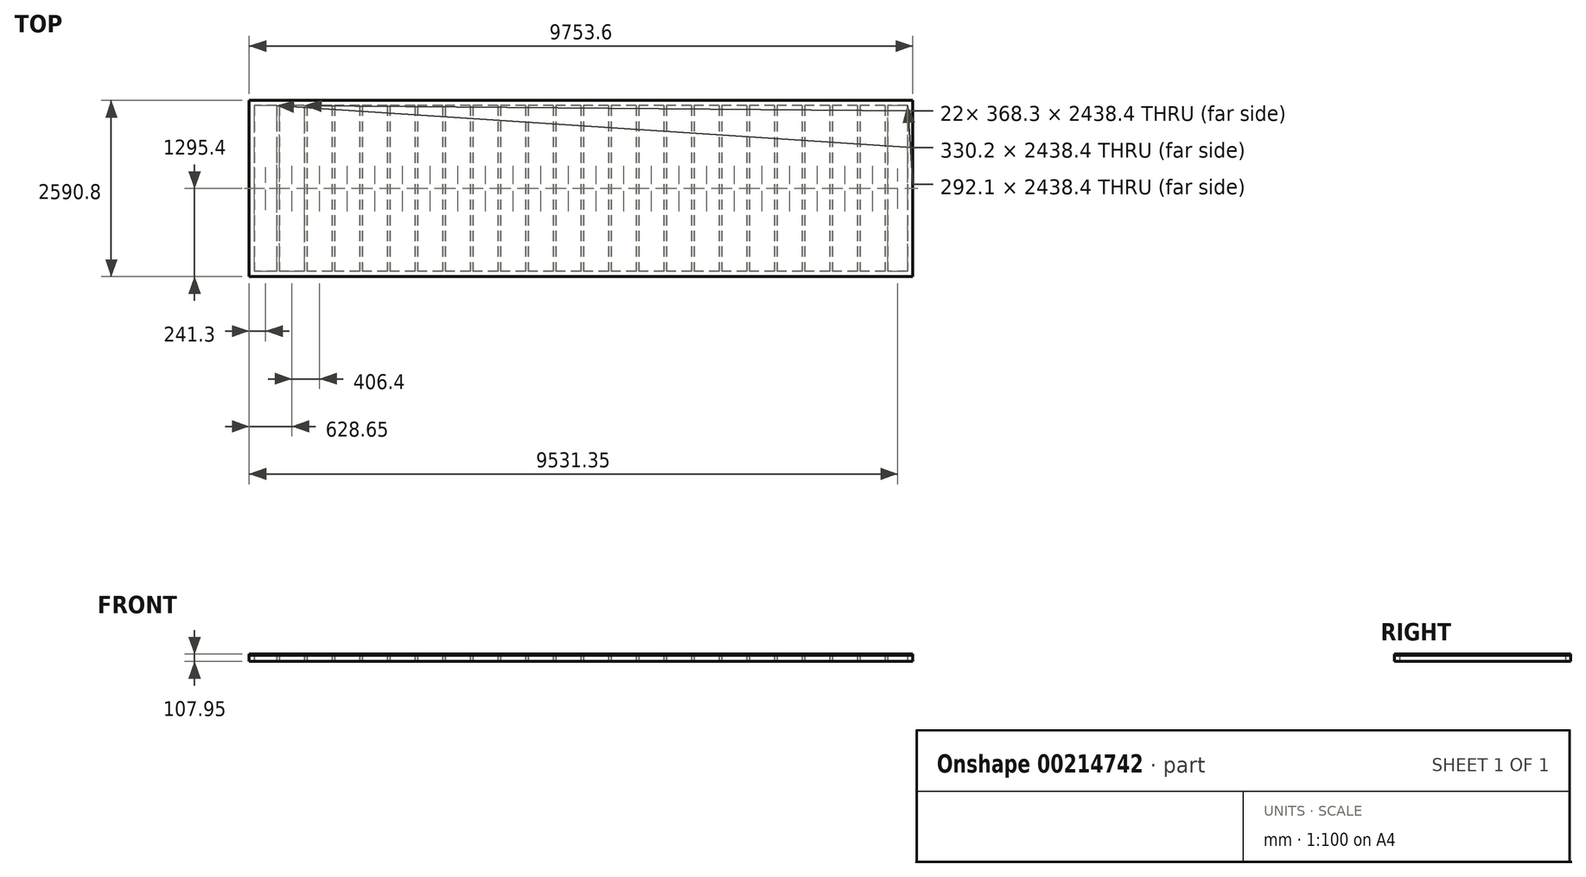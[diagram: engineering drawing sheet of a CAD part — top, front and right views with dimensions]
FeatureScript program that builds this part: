
annotation { "Feature Type Name" : "Feature", "Feature Type Description" : "" }
export const myFeature = defineFeature(function(context is Context, id is Id, definition is map)
    precondition{}
    {
        {
            var Q0;
            Q0=qCreatedBy(makeId("Right.planeOp"),FACE);
            var sketch = newSketch(context, id + "F0", { "sketchPlane" : qUnion([Q0])});
            skLineSegment(sketch, "E0.bottom", {"start": v(19.05, -44.45) * mm, "end": v(-19.05, -44.45) * mm});
            skLineSegment(sketch, "E0.top", {"start": v(19.05, 44.45) * mm, "end": v(-19.05, 44.45) * mm});
            skLineSegment(sketch, "E0.left", {"start": v(19.05, -44.45) * mm, "end": v(19.05, 44.45) * mm});
            skLineSegment(sketch, "E0.right", {"start": v(-19.05, -44.45) * mm, "end": v(-19.05, 44.45) * mm});
            skPoint(sketch, "E0.middle", {"position": v(0, 0) * mm});
            skSolve(sketch);
        }
        {
            var Q0;
            Q0 = qSketchRegion(id + "F0", true);
            extrude(context, id + "F1", {"entities" : qUnion([Q0]), "depth" : 9753.6 * mm, "offsetDistance" : 25.4 * mm});
        }
        {
            var Q0;
            Q0=makeQuery(id+"F1.opExtrude","SWEPT_FACE",FACE,{"disambiguationData":[OSD([sQuery(id+"F0.wireOp",EDGE,"E0.left")])]});
            var sketch = newSketch(context, id + "F2", { "sketchPlane" : qUnion([Q0])});
            skLineSegment(sketch, "E1.bottom", {"start": v(0, 44.45) * mm, "end": v(-38.1, 44.45) * mm});
            skLineSegment(sketch, "E1.top", {"start": v(0, -44.45) * mm, "end": v(-38.1, -44.45) * mm});
            skLineSegment(sketch, "E1.left", {"start": v(0, 44.45) * mm, "end": v(0, -44.45) * mm});
            skLineSegment(sketch, "E1.right", {"start": v(-38.1, 44.45) * mm, "end": v(-38.1, -44.45) * mm});
            skLineSegment(sketch, "E2.1.0.0", {"start": v(-444.5, 44.45) * mm, "end": v(-444.5, -44.45) * mm});
            skLineSegment(sketch, "E2.1.0.1", {"start": v(-406.4, -44.45) * mm, "end": v(-444.5, -44.45) * mm});
            skLineSegment(sketch, "E2.1.0.2", {"start": v(-406.4, 44.45) * mm, "end": v(-406.4, -44.45) * mm});
            skLineSegment(sketch, "E2.1.0.3", {"start": v(-406.4, 44.45) * mm, "end": v(-444.5, 44.45) * mm});
            skLineSegment(sketch, "E2.2.0.0", {"start": v(-850.9, 44.45) * mm, "end": v(-850.9, -44.45) * mm});
            skLineSegment(sketch, "E2.2.0.1", {"start": v(-812.8, -44.45) * mm, "end": v(-850.9, -44.45) * mm});
            skLineSegment(sketch, "E2.2.0.2", {"start": v(-812.8, 44.45) * mm, "end": v(-812.8, -44.45) * mm});
            skLineSegment(sketch, "E2.2.0.3", {"start": v(-812.8, 44.45) * mm, "end": v(-850.9, 44.45) * mm});
            skLineSegment(sketch, "E2.3.0.0", {"start": v(-1257.3, 44.45) * mm, "end": v(-1257.3, -44.45) * mm});
            skLineSegment(sketch, "E2.3.0.1", {"start": v(-1219.2, -44.45) * mm, "end": v(-1257.3, -44.45) * mm});
            skLineSegment(sketch, "E2.3.0.2", {"start": v(-1219.2, 44.45) * mm, "end": v(-1219.2, -44.45) * mm});
            skLineSegment(sketch, "E2.3.0.3", {"start": v(-1219.2, 44.45) * mm, "end": v(-1257.3, 44.45) * mm});
            skLineSegment(sketch, "E2.4.0.0", {"start": v(-1663.7, 44.45) * mm, "end": v(-1663.7, -44.45) * mm});
            skLineSegment(sketch, "E2.4.0.1", {"start": v(-1625.6, -44.45) * mm, "end": v(-1663.7, -44.45) * mm});
            skLineSegment(sketch, "E2.4.0.2", {"start": v(-1625.6, 44.45) * mm, "end": v(-1625.6, -44.45) * mm});
            skLineSegment(sketch, "E2.4.0.3", {"start": v(-1625.6, 44.45) * mm, "end": v(-1663.7, 44.45) * mm});
            skLineSegment(sketch, "E2.5.0.0", {"start": v(-2070.1, 44.45) * mm, "end": v(-2070.1, -44.45) * mm});
            skLineSegment(sketch, "E2.5.0.1", {"start": v(-2032, -44.45) * mm, "end": v(-2070.1, -44.45) * mm});
            skLineSegment(sketch, "E2.5.0.2", {"start": v(-2032, 44.45) * mm, "end": v(-2032, -44.45) * mm});
            skLineSegment(sketch, "E2.5.0.3", {"start": v(-2032, 44.45) * mm, "end": v(-2070.1, 44.45) * mm});
            skLineSegment(sketch, "E2.6.0.0", {"start": v(-2476.5, 44.45) * mm, "end": v(-2476.5, -44.45) * mm});
            skLineSegment(sketch, "E2.6.0.1", {"start": v(-2438.4, -44.45) * mm, "end": v(-2476.5, -44.45) * mm});
            skLineSegment(sketch, "E2.6.0.2", {"start": v(-2438.4, 44.45) * mm, "end": v(-2438.4, -44.45) * mm});
            skLineSegment(sketch, "E2.6.0.3", {"start": v(-2438.4, 44.45) * mm, "end": v(-2476.5, 44.45) * mm});
            skLineSegment(sketch, "E2.7.0.0", {"start": v(-2882.9, 44.45) * mm, "end": v(-2882.9, -44.45) * mm});
            skLineSegment(sketch, "E2.7.0.1", {"start": v(-2844.8, -44.45) * mm, "end": v(-2882.9, -44.45) * mm});
            skLineSegment(sketch, "E2.7.0.2", {"start": v(-2844.8, 44.45) * mm, "end": v(-2844.8, -44.45) * mm});
            skLineSegment(sketch, "E2.7.0.3", {"start": v(-2844.8, 44.45) * mm, "end": v(-2882.9, 44.45) * mm});
            skLineSegment(sketch, "E2.8.0.0", {"start": v(-3289.3, 44.45) * mm, "end": v(-3289.3, -44.45) * mm});
            skLineSegment(sketch, "E2.8.0.1", {"start": v(-3251.2, -44.45) * mm, "end": v(-3289.3, -44.45) * mm});
            skLineSegment(sketch, "E2.8.0.2", {"start": v(-3251.2, 44.45) * mm, "end": v(-3251.2, -44.45) * mm});
            skLineSegment(sketch, "E2.8.0.3", {"start": v(-3251.2, 44.45) * mm, "end": v(-3289.3, 44.45) * mm});
            skLineSegment(sketch, "E2.9.0.0", {"start": v(-3695.7, 44.45) * mm, "end": v(-3695.7, -44.45) * mm});
            skLineSegment(sketch, "E2.9.0.1", {"start": v(-3657.6, -44.45) * mm, "end": v(-3695.7, -44.45) * mm});
            skLineSegment(sketch, "E2.9.0.2", {"start": v(-3657.6, 44.45) * mm, "end": v(-3657.6, -44.45) * mm});
            skLineSegment(sketch, "E2.9.0.3", {"start": v(-3657.6, 44.45) * mm, "end": v(-3695.7, 44.45) * mm});
            skLineSegment(sketch, "E2.10.0.0", {"start": v(-4102.1, 44.45) * mm, "end": v(-4102.1, -44.45) * mm});
            skLineSegment(sketch, "E2.10.0.1", {"start": v(-4064, -44.45) * mm, "end": v(-4102.1, -44.45) * mm});
            skLineSegment(sketch, "E2.10.0.2", {"start": v(-4064, 44.45) * mm, "end": v(-4064, -44.45) * mm});
            skLineSegment(sketch, "E2.10.0.3", {"start": v(-4064, 44.45) * mm, "end": v(-4102.1, 44.45) * mm});
            skLineSegment(sketch, "E2.11.0.0", {"start": v(-4508.5, 44.45) * mm, "end": v(-4508.5, -44.45) * mm});
            skLineSegment(sketch, "E2.11.0.1", {"start": v(-4470.4, -44.45) * mm, "end": v(-4508.5, -44.45) * mm});
            skLineSegment(sketch, "E2.11.0.2", {"start": v(-4470.4, 44.45) * mm, "end": v(-4470.4, -44.45) * mm});
            skLineSegment(sketch, "E2.11.0.3", {"start": v(-4470.4, 44.45) * mm, "end": v(-4508.5, 44.45) * mm});
            skLineSegment(sketch, "E2.12.0.0", {"start": v(-4914.9, 44.45) * mm, "end": v(-4914.9, -44.45) * mm});
            skLineSegment(sketch, "E2.12.0.1", {"start": v(-4876.8, -44.45) * mm, "end": v(-4914.9, -44.45) * mm});
            skLineSegment(sketch, "E2.12.0.2", {"start": v(-4876.8, 44.45) * mm, "end": v(-4876.8, -44.45) * mm});
            skLineSegment(sketch, "E2.12.0.3", {"start": v(-4876.8, 44.45) * mm, "end": v(-4914.9, 44.45) * mm});
            skLineSegment(sketch, "E2.13.0.0", {"start": v(-5321.3, 44.45) * mm, "end": v(-5321.3, -44.45) * mm});
            skLineSegment(sketch, "E2.13.0.1", {"start": v(-5283.2, -44.45) * mm, "end": v(-5321.3, -44.45) * mm});
            skLineSegment(sketch, "E2.13.0.2", {"start": v(-5283.2, 44.45) * mm, "end": v(-5283.2, -44.45) * mm});
            skLineSegment(sketch, "E2.13.0.3", {"start": v(-5283.2, 44.45) * mm, "end": v(-5321.3, 44.45) * mm});
            skLineSegment(sketch, "E2.14.0.0", {"start": v(-5727.7, 44.45) * mm, "end": v(-5727.7, -44.45) * mm});
            skLineSegment(sketch, "E2.14.0.1", {"start": v(-5689.6, -44.45) * mm, "end": v(-5727.7, -44.45) * mm});
            skLineSegment(sketch, "E2.14.0.2", {"start": v(-5689.6, 44.45) * mm, "end": v(-5689.6, -44.45) * mm});
            skLineSegment(sketch, "E2.14.0.3", {"start": v(-5689.6, 44.45) * mm, "end": v(-5727.7, 44.45) * mm});
            skLineSegment(sketch, "E2.15.0.0", {"start": v(-6134.1, 44.45) * mm, "end": v(-6134.1, -44.45) * mm});
            skLineSegment(sketch, "E2.15.0.1", {"start": v(-6096, -44.45) * mm, "end": v(-6134.1, -44.45) * mm});
            skLineSegment(sketch, "E2.15.0.2", {"start": v(-6096, 44.45) * mm, "end": v(-6096, -44.45) * mm});
            skLineSegment(sketch, "E2.15.0.3", {"start": v(-6096, 44.45) * mm, "end": v(-6134.1, 44.45) * mm});
            skLineSegment(sketch, "E2.16.0.0", {"start": v(-6540.5, 44.45) * mm, "end": v(-6540.5, -44.45) * mm});
            skLineSegment(sketch, "E2.16.0.1", {"start": v(-6502.4, -44.45) * mm, "end": v(-6540.5, -44.45) * mm});
            skLineSegment(sketch, "E2.16.0.2", {"start": v(-6502.4, 44.45) * mm, "end": v(-6502.4, -44.45) * mm});
            skLineSegment(sketch, "E2.16.0.3", {"start": v(-6502.4, 44.45) * mm, "end": v(-6540.5, 44.45) * mm});
            skLineSegment(sketch, "E2.17.0.0", {"start": v(-6946.9, 44.45) * mm, "end": v(-6946.9, -44.45) * mm});
            skLineSegment(sketch, "E2.17.0.1", {"start": v(-6908.8, -44.45) * mm, "end": v(-6946.9, -44.45) * mm});
            skLineSegment(sketch, "E2.17.0.2", {"start": v(-6908.8, 44.45) * mm, "end": v(-6908.8, -44.45) * mm});
            skLineSegment(sketch, "E2.17.0.3", {"start": v(-6908.8, 44.45) * mm, "end": v(-6946.9, 44.45) * mm});
            skLineSegment(sketch, "E2.18.0.0", {"start": v(-7353.3, 44.45) * mm, "end": v(-7353.3, -44.45) * mm});
            skLineSegment(sketch, "E2.18.0.1", {"start": v(-7315.2, -44.45) * mm, "end": v(-7353.3, -44.45) * mm});
            skLineSegment(sketch, "E2.18.0.2", {"start": v(-7315.2, 44.45) * mm, "end": v(-7315.2, -44.45) * mm});
            skLineSegment(sketch, "E2.18.0.3", {"start": v(-7315.2, 44.45) * mm, "end": v(-7353.3, 44.45) * mm});
            skLineSegment(sketch, "E2.19.0.0", {"start": v(-7759.7, 44.45) * mm, "end": v(-7759.7, -44.45) * mm});
            skLineSegment(sketch, "E2.19.0.1", {"start": v(-7721.6, -44.45) * mm, "end": v(-7759.7, -44.45) * mm});
            skLineSegment(sketch, "E2.19.0.2", {"start": v(-7721.6, 44.45) * mm, "end": v(-7721.6, -44.45) * mm});
            skLineSegment(sketch, "E2.19.0.3", {"start": v(-7721.6, 44.45) * mm, "end": v(-7759.7, 44.45) * mm});
            skLineSegment(sketch, "E2.20.0.0", {"start": v(-8166.1, 44.45) * mm, "end": v(-8166.1, -44.45) * mm});
            skLineSegment(sketch, "E2.20.0.1", {"start": v(-8128, -44.45) * mm, "end": v(-8166.1, -44.45) * mm});
            skLineSegment(sketch, "E2.20.0.2", {"start": v(-8128, 44.45) * mm, "end": v(-8128, -44.45) * mm});
            skLineSegment(sketch, "E2.20.0.3", {"start": v(-8128, 44.45) * mm, "end": v(-8166.1, 44.45) * mm});
            skLineSegment(sketch, "E2.21.0.0", {"start": v(-8572.5, 44.45) * mm, "end": v(-8572.5, -44.45) * mm});
            skLineSegment(sketch, "E2.21.0.1", {"start": v(-8534.4, -44.45) * mm, "end": v(-8572.5, -44.45) * mm});
            skLineSegment(sketch, "E2.21.0.2", {"start": v(-8534.4, 44.45) * mm, "end": v(-8534.4, -44.45) * mm});
            skLineSegment(sketch, "E2.21.0.3", {"start": v(-8534.4, 44.45) * mm, "end": v(-8572.5, 44.45) * mm});
            skLineSegment(sketch, "E2.22.0.0", {"start": v(-8978.9, 44.45) * mm, "end": v(-8978.9, -44.45) * mm});
            skLineSegment(sketch, "E2.22.0.1", {"start": v(-8940.8, -44.45) * mm, "end": v(-8978.9, -44.45) * mm});
            skLineSegment(sketch, "E2.22.0.2", {"start": v(-8940.8, 44.45) * mm, "end": v(-8940.8, -44.45) * mm});
            skLineSegment(sketch, "E2.22.0.3", {"start": v(-8940.8, 44.45) * mm, "end": v(-8978.9, 44.45) * mm});
            skLineSegment(sketch, "E2.23.0.0", {"start": v(-9385.3, 44.45) * mm, "end": v(-9385.3, -44.45) * mm});
            skLineSegment(sketch, "E2.23.0.1", {"start": v(-9347.2, -44.45) * mm, "end": v(-9385.3, -44.45) * mm});
            skLineSegment(sketch, "E2.23.0.2", {"start": v(-9347.2, 44.45) * mm, "end": v(-9347.2, -44.45) * mm});
            skLineSegment(sketch, "E2.23.0.3", {"start": v(-9347.2, 44.45) * mm, "end": v(-9385.3, 44.45) * mm});
            skLineSegment(sketch, "E2.direction1", {"start": v(-38.1, -44.45) * mm, "end": v(-444.5, -44.45) * mm, "construction": true});
            skSolve(sketch);
        }
        {
            var Q0;
            Q0=makeQuery(id+"F2.imprint","IMPRINT",FACE,{"disambiguationData":[TD([[makeQuery(id+"F2.imprint","IMPRINT",EDGE,{"derivedFrom":sQuery(id+"F2.wireOp",EDGE,"E2.23.0.0")}),1.0]])]});
            var Q1;
            Q1=makeQuery(id+"F2.imprint","IMPRINT",FACE,{"disambiguationData":[TD([[makeQuery(id+"F2.imprint","IMPRINT",EDGE,{"derivedFrom":sQuery(id+"F2.wireOp",EDGE,"E2.22.0.0")}),1.0]])]});
            var Q2;
            Q2=makeQuery(id+"F2.imprint","IMPRINT",FACE,{"disambiguationData":[TD([[makeQuery(id+"F2.imprint","IMPRINT",EDGE,{"derivedFrom":sQuery(id+"F2.wireOp",EDGE,"E2.21.0.0")}),1.0]])]});
            var Q3;
            Q3=makeQuery(id+"F2.imprint","IMPRINT",FACE,{"disambiguationData":[TD([[makeQuery(id+"F2.imprint","IMPRINT",EDGE,{"derivedFrom":sQuery(id+"F2.wireOp",EDGE,"E2.20.0.0")}),1.0]])]});
            var Q4;
            Q4=makeQuery(id+"F2.imprint","IMPRINT",FACE,{"disambiguationData":[TD([[makeQuery(id+"F2.imprint","IMPRINT",EDGE,{"derivedFrom":sQuery(id+"F2.wireOp",EDGE,"E2.19.0.0")}),1.0]])]});
            var Q5;
            Q5=makeQuery(id+"F2.imprint","IMPRINT",FACE,{"disambiguationData":[TD([[makeQuery(id+"F2.imprint","IMPRINT",EDGE,{"derivedFrom":sQuery(id+"F2.wireOp",EDGE,"E2.18.0.0")}),1.0]])]});
            var Q6;
            Q6=makeQuery(id+"F2.imprint","IMPRINT",FACE,{"disambiguationData":[TD([[makeQuery(id+"F2.imprint","IMPRINT",EDGE,{"derivedFrom":sQuery(id+"F2.wireOp",EDGE,"E2.17.0.0")}),1.0]])]});
            var Q7;
            Q7=makeQuery(id+"F2.imprint","IMPRINT",FACE,{"disambiguationData":[TD([[makeQuery(id+"F2.imprint","IMPRINT",EDGE,{"derivedFrom":sQuery(id+"F2.wireOp",EDGE,"E2.16.0.0")}),1.0]])]});
            var Q8;
            Q8=makeQuery(id+"F2.imprint","IMPRINT",FACE,{"disambiguationData":[TD([[makeQuery(id+"F2.imprint","IMPRINT",EDGE,{"derivedFrom":sQuery(id+"F2.wireOp",EDGE,"E2.15.0.0")}),1.0]])]});
            var Q9;
            Q9=makeQuery(id+"F2.imprint","IMPRINT",FACE,{"disambiguationData":[TD([[makeQuery(id+"F2.imprint","IMPRINT",EDGE,{"derivedFrom":sQuery(id+"F2.wireOp",EDGE,"E2.14.0.0")}),1.0]])]});
            var Q10;
            Q10=makeQuery(id+"F2.imprint","IMPRINT",FACE,{"disambiguationData":[TD([[makeQuery(id+"F2.imprint","IMPRINT",EDGE,{"derivedFrom":sQuery(id+"F2.wireOp",EDGE,"E2.13.0.0")}),1.0]])]});
            var Q11;
            Q11=makeQuery(id+"F2.imprint","IMPRINT",FACE,{"disambiguationData":[TD([[makeQuery(id+"F2.imprint","IMPRINT",EDGE,{"derivedFrom":sQuery(id+"F2.wireOp",EDGE,"E2.12.0.0")}),1.0]])]});
            var Q12;
            Q12=makeQuery(id+"F2.imprint","IMPRINT",FACE,{"disambiguationData":[TD([[makeQuery(id+"F2.imprint","IMPRINT",EDGE,{"derivedFrom":sQuery(id+"F2.wireOp",EDGE,"E2.11.0.0")}),1.0]])]});
            var Q13;
            Q13=makeQuery(id+"F2.imprint","IMPRINT",FACE,{"disambiguationData":[TD([[makeQuery(id+"F2.imprint","IMPRINT",EDGE,{"derivedFrom":sQuery(id+"F2.wireOp",EDGE,"E2.10.0.0")}),1.0]])]});
            var Q14;
            Q14=makeQuery(id+"F2.imprint","IMPRINT",FACE,{"disambiguationData":[TD([[makeQuery(id+"F2.imprint","IMPRINT",EDGE,{"derivedFrom":sQuery(id+"F2.wireOp",EDGE,"E2.9.0.0")}),1.0]])]});
            var Q15;
            Q15=makeQuery(id+"F2.imprint","IMPRINT",FACE,{"disambiguationData":[TD([[makeQuery(id+"F2.imprint","IMPRINT",EDGE,{"derivedFrom":sQuery(id+"F2.wireOp",EDGE,"E2.8.0.0")}),1.0]])]});
            var Q16;
            Q16=makeQuery(id+"F2.imprint","IMPRINT",FACE,{"disambiguationData":[TD([[makeQuery(id+"F2.imprint","IMPRINT",EDGE,{"derivedFrom":sQuery(id+"F2.wireOp",EDGE,"E2.7.0.0")}),1.0]])]});
            var Q17;
            Q17=makeQuery(id+"F2.imprint","IMPRINT",FACE,{"disambiguationData":[TD([[makeQuery(id+"F2.imprint","IMPRINT",EDGE,{"derivedFrom":sQuery(id+"F2.wireOp",EDGE,"E2.6.0.0")}),1.0]])]});
            var Q18;
            Q18=makeQuery(id+"F2.imprint","IMPRINT",FACE,{"disambiguationData":[TD([[makeQuery(id+"F2.imprint","IMPRINT",EDGE,{"derivedFrom":sQuery(id+"F2.wireOp",EDGE,"E2.5.0.0")}),1.0]])]});
            var Q19;
            Q19=makeQuery(id+"F2.imprint","IMPRINT",FACE,{"disambiguationData":[TD([[makeQuery(id+"F2.imprint","IMPRINT",EDGE,{"derivedFrom":sQuery(id+"F2.wireOp",EDGE,"E2.4.0.0")}),1.0]])]});
            var Q20;
            Q20=makeQuery(id+"F2.imprint","IMPRINT",FACE,{"disambiguationData":[TD([[makeQuery(id+"F2.imprint","IMPRINT",EDGE,{"derivedFrom":sQuery(id+"F2.wireOp",EDGE,"E2.3.0.0")}),1.0]])]});
            var Q21;
            Q21=makeQuery(id+"F2.imprint","IMPRINT",FACE,{"disambiguationData":[TD([[makeQuery(id+"F2.imprint","IMPRINT",EDGE,{"derivedFrom":sQuery(id+"F2.wireOp",EDGE,"E2.2.0.0")}),1.0]])]});
            var Q22;
            Q22=makeQuery(id+"F2.imprint","IMPRINT",FACE,{"disambiguationData":[TD([[makeQuery(id+"F2.imprint","IMPRINT",EDGE,{"derivedFrom":sQuery(id+"F2.wireOp",EDGE,"E2.1.0.0")}),1.0]])]});
            var Q23;
            Q23=makeQuery(id+"F2.imprint","IMPRINT",FACE,{"disambiguationData":[TD([[makeQuery(id+"F2.imprint","IMPRINT",EDGE,{"derivedFrom":sQuery(id+"F2.wireOp",EDGE,"E1.bottom")}),-1.0]])]});
            extrude(context, id + "F3", {"entities" : qUnion([Q0, Q1, Q2, Q3, Q4, Q5, Q6, Q7, Q8, Q9, Q10, Q11, Q12, Q13, Q14, Q15, Q16, Q17, Q18, Q19, Q20, Q21, Q22, Q23]), "operationType" : NewBodyOperationType.ADD, "depth" : 2438.4 * mm, "offsetDistance" : 25.4 * mm});
        }
        {
            var Q0;
            {var subQ0=sQuery(id+"F0.wireOp",EDGE,"E0.left");Q0=makeQuery(id+"F3.boolean.opBoolean","SPLIT",FACE,{"disambiguationData":[TD([makeQuery(id+"F3.opExtrude","SWEPT_FACE",FACE,{"disambiguationData":[OSD([sQuery(id+"F2.wireOp",EDGE,"E2.23.0.0")])]})])],"derivedFrom":makeQuery(id+"F1.opExtrude","SWEPT_FACE",FACE,{"disambiguationData":[OSD([subQ0])]})});}
            var sketch = newSketch(context, id + "F4", { "sketchPlane" : qUnion([Q0])});
            skLineSegment(sketch, "E3.bottom", {"start": v(-9753.6, 44.45) * mm, "end": v(-9677.4, 44.45) * mm});
            skLineSegment(sketch, "E3.top", {"start": v(-9753.6, -44.45) * mm, "end": v(-9677.4, -44.45) * mm});
            skLineSegment(sketch, "E3.left", {"start": v(-9753.6, 44.45) * mm, "end": v(-9753.6, -44.45) * mm});
            skLineSegment(sketch, "E3.right", {"start": v(-9677.4, 44.45) * mm, "end": v(-9677.4, -44.45) * mm});
            skSolve(sketch);
        }
        {
            var Q0;
            Q0 = qSketchRegion(id + "F4", true);
            extrude(context, id + "F5", {"entities" : qUnion([Q0]), "operationType" : NewBodyOperationType.ADD, "depth" : 2438.4 * mm, "offsetDistance" : 25.4 * mm});
        }
        {
            var Q0;
            Q0=makeQuery(id+"F3.boolean.opBoolean","SPLIT",FACE,{"disambiguationData":[TD([makeQuery(id+"F3.opExtrude","SWEPT_FACE",FACE,{"disambiguationData":[OSD([sQuery(id+"F2.wireOp",EDGE,"E1.right")])]})])],"derivedFrom":makeQuery(id+"F1.opExtrude","SWEPT_FACE",FACE,{"disambiguationData":[OSD([sQuery(id+"F0.wireOp",EDGE,"E0.left")])]})});
            var sketch = newSketch(context, id + "F6", { "sketchPlane" : qUnion([Q0])});
            skLineSegment(sketch, "E4.bottom", {"start": v(-38.1, 44.45) * mm, "end": v(-76.2, 44.45) * mm});
            skLineSegment(sketch, "E4.top", {"start": v(-38.1, -44.45) * mm, "end": v(-76.2, -44.45) * mm});
            skLineSegment(sketch, "E4.left", {"start": v(-38.1, 44.45) * mm, "end": v(-38.1, -44.45) * mm});
            skLineSegment(sketch, "E4.right", {"start": v(-76.2, 44.45) * mm, "end": v(-76.2, -44.45) * mm});
            skSolve(sketch);
        }
        {
            var Q0;
            Q0 = qSketchRegion(id + "F6", true);
            extrude(context, id + "F7", {"entities" : qUnion([Q0]), "operationType" : NewBodyOperationType.ADD, "depth" : 2438.4 * mm, "offsetDistance" : 25.4 * mm});
        }
        {
            var Q0;
            Q0=makeQuery(id+"F1.opExtrude","SWEPT_FACE",FACE,{"disambiguationData":[OSD([sQuery(id+"F0.wireOp",EDGE,"E0.right")])]});
            extrude(context, id + "F8", {"entities" : qUnion([Q0]), "operationType" : NewBodyOperationType.ADD, "depth" : 38.1 * mm, "offsetDistance" : 25.4 * mm});
        }
        {
            var Q0;
            {var subQ0=sQuery(id+"F0.wireOp",EDGE,"E0.right");Q0=makeQuery(id+"F8.boolean.opBoolean","MERGE",FACE,{"derivedFrom":[makeQuery(id+"F3.boolean.opBoolean","MERGE",FACE,{"derivedFrom":[makeQuery(id+"F1.opExtrude","CAP_FACE",FACE,{"disambiguationData":[OSD([sQuery(id+"F0.wireOp",EDGE,"E0.bottom"),sQuery(id+"F0.wireOp",EDGE,"E0.top"),sQuery(id+"F0.wireOp",EDGE,"E0.left"),subQ0])],"isStart":true}),makeQuery(id+"F3.opExtrude","SWEPT_FACE",FACE,{"disambiguationData":[OSD([sQuery(id+"F2.wireOp",EDGE,"E1.left")])]})]}),makeQuery(id+"F8.opExtrude","SWEPT_FACE",FACE,{"disambiguationData":[OSD([subQ0]),TDD([makeQuery(id+"F1.opExtrude","CAP_EDGE",EDGE,{"disambiguationData":[OSD([subQ0])],"isStart":true})])]})]});}
            var sketch = newSketch(context, id + "F9", { "sketchPlane" : qUnion([Q0])});
            skLineSegment(sketch, "E5.bottom", {"start": v(-2457.45, 44.45) * mm, "end": v(-2533.65, 44.45) * mm});
            skLineSegment(sketch, "E5.top", {"start": v(-2457.45, -44.45) * mm, "end": v(-2533.65, -44.45) * mm});
            skLineSegment(sketch, "E5.left", {"start": v(-2457.45, 44.45) * mm, "end": v(-2457.45, -44.45) * mm});
            skLineSegment(sketch, "E5.right", {"start": v(-2533.65, 44.45) * mm, "end": v(-2533.65, -44.45) * mm});
            skSolve(sketch);
        }
        {
            var Q0;
            Q0 = qSketchRegion(id + "F9", true);
            extrude(context, id + "F10", {"entities" : qUnion([Q0]), "operationType" : NewBodyOperationType.ADD, "oppositeDirection" : true, "depth" : 9753.6 * mm, "offsetDistance" : 25.4 * mm});
        }
        {
            var Q0;
            {var subQ0=sQuery(id+"F0.wireOp",EDGE,"E0.top");Q0=makeQuery(id+"F10.boolean.opBoolean","MERGE",FACE,{"derivedFrom":[makeQuery(id+"F8.boolean.opBoolean","MERGE",FACE,{"derivedFrom":[makeQuery(id+"F7.boolean.opBoolean","MERGE",FACE,{"derivedFrom":[makeQuery(id+"F5.boolean.opBoolean","MERGE",FACE,{"derivedFrom":[makeQuery(id+"F3.boolean.opBoolean","MERGE",FACE,{"derivedFrom":[makeQuery(id+"F1.opExtrude","SWEPT_FACE",FACE,{"disambiguationData":[OSD([subQ0])]}),makeQuery(id+"F3.opExtrude","SWEPT_FACE",FACE,{"disambiguationData":[OSD([sQuery(id+"F2.wireOp",EDGE,"E1.bottom")])]}),makeQuery(id+"F3.opExtrude","SWEPT_FACE",FACE,{"disambiguationData":[OSD([sQuery(id+"F2.wireOp",EDGE,"E2.1.0.3")])]}),makeQuery(id+"F3.opExtrude","SWEPT_FACE",FACE,{"disambiguationData":[OSD([sQuery(id+"F2.wireOp",EDGE,"E2.2.0.3")])]}),makeQuery(id+"F3.opExtrude","SWEPT_FACE",FACE,{"disambiguationData":[OSD([sQuery(id+"F2.wireOp",EDGE,"E2.3.0.3")])]}),makeQuery(id+"F3.opExtrude","SWEPT_FACE",FACE,{"disambiguationData":[OSD([sQuery(id+"F2.wireOp",EDGE,"E2.4.0.3")])]}),makeQuery(id+"F3.opExtrude","SWEPT_FACE",FACE,{"disambiguationData":[OSD([sQuery(id+"F2.wireOp",EDGE,"E2.5.0.3")])]}),makeQuery(id+"F3.opExtrude","SWEPT_FACE",FACE,{"disambiguationData":[OSD([sQuery(id+"F2.wireOp",EDGE,"E2.6.0.3")])]}),makeQuery(id+"F3.opExtrude","SWEPT_FACE",FACE,{"disambiguationData":[OSD([sQuery(id+"F2.wireOp",EDGE,"E2.7.0.3")])]}),makeQuery(id+"F3.opExtrude","SWEPT_FACE",FACE,{"disambiguationData":[OSD([sQuery(id+"F2.wireOp",EDGE,"E2.8.0.3")])]}),makeQuery(id+"F3.opExtrude","SWEPT_FACE",FACE,{"disambiguationData":[OSD([sQuery(id+"F2.wireOp",EDGE,"E2.9.0.3")])]}),makeQuery(id+"F3.opExtrude","SWEPT_FACE",FACE,{"disambiguationData":[OSD([sQuery(id+"F2.wireOp",EDGE,"E2.10.0.3")])]}),makeQuery(id+"F3.opExtrude","SWEPT_FACE",FACE,{"disambiguationData":[OSD([sQuery(id+"F2.wireOp",EDGE,"E2.11.0.3")])]}),makeQuery(id+"F3.opExtrude","SWEPT_FACE",FACE,{"disambiguationData":[OSD([sQuery(id+"F2.wireOp",EDGE,"E2.12.0.3")])]}),makeQuery(id+"F3.opExtrude","SWEPT_FACE",FACE,{"disambiguationData":[OSD([sQuery(id+"F2.wireOp",EDGE,"E2.13.0.3")])]}),makeQuery(id+"F3.opExtrude","SWEPT_FACE",FACE,{"disambiguationData":[OSD([sQuery(id+"F2.wireOp",EDGE,"E2.14.0.3")])]}),makeQuery(id+"F3.opExtrude","SWEPT_FACE",FACE,{"disambiguationData":[OSD([sQuery(id+"F2.wireOp",EDGE,"E2.15.0.3")])]}),makeQuery(id+"F3.opExtrude","SWEPT_FACE",FACE,{"disambiguationData":[OSD([sQuery(id+"F2.wireOp",EDGE,"E2.16.0.3")])]}),makeQuery(id+"F3.opExtrude","SWEPT_FACE",FACE,{"disambiguationData":[OSD([sQuery(id+"F2.wireOp",EDGE,"E2.17.0.3")])]}),makeQuery(id+"F3.opExtrude","SWEPT_FACE",FACE,{"disambiguationData":[OSD([sQuery(id+"F2.wireOp",EDGE,"E2.18.0.3")])]}),makeQuery(id+"F3.opExtrude","SWEPT_FACE",FACE,{"disambiguationData":[OSD([sQuery(id+"F2.wireOp",EDGE,"E2.19.0.3")])]}),makeQuery(id+"F3.opExtrude","SWEPT_FACE",FACE,{"disambiguationData":[OSD([sQuery(id+"F2.wireOp",EDGE,"E2.20.0.3")])]}),makeQuery(id+"F3.opExtrude","SWEPT_FACE",FACE,{"disambiguationData":[OSD([sQuery(id+"F2.wireOp",EDGE,"E2.21.0.3")])]}),makeQuery(id+"F3.opExtrude","SWEPT_FACE",FACE,{"disambiguationData":[OSD([sQuery(id+"F2.wireOp",EDGE,"E2.22.0.3")])]}),makeQuery(id+"F3.opExtrude","SWEPT_FACE",FACE,{"disambiguationData":[OSD([sQuery(id+"F2.wireOp",EDGE,"E2.23.0.3")])]})]}),makeQuery(id+"F5.opExtrude","SWEPT_FACE",FACE,{"disambiguationData":[OSD([sQuery(id+"F4.wireOp",EDGE,"E3.bottom")])]})]}),makeQuery(id+"F7.opExtrude","SWEPT_FACE",FACE,{"disambiguationData":[OSD([sQuery(id+"F6.wireOp",EDGE,"E4.bottom")])]})]}),makeQuery(id+"F8.opExtrude","SWEPT_FACE",FACE,{"disambiguationData":[OSD([subQ0,sQuery(id+"F0.wireOp",EDGE,"E0.right")])]})]}),makeQuery(id+"F10.opExtrude","SWEPT_FACE",FACE,{"disambiguationData":[OSD([sQuery(id+"F9.wireOp",EDGE,"E5.bottom")])]})]});}
            var sketch = newSketch(context, id + "F11", { "sketchPlane" : qUnion([Q0])});
            skLineSegment(sketch, "E6.bottom", {"start": v(0, 2533.65) * mm, "end": v(9753.6, 2533.65) * mm});
            skLineSegment(sketch, "E6.top", {"start": v(0, -57.15) * mm, "end": v(9753.6, -57.15) * mm});
            skLineSegment(sketch, "E6.left", {"start": v(0, 2533.65) * mm, "end": v(0, -57.15) * mm});
            skLineSegment(sketch, "E6.right", {"start": v(9753.6, 2533.65) * mm, "end": v(9753.6, -57.15) * mm});
            skSolve(sketch);
        }
        {
            var Q0;
            Q0 = qSketchRegion(id + "F11", true);
            extrude(context, id + "F12", {"entities" : qUnion([Q0]), "depth" : 19.05 * mm, "offsetDistance" : 25.4 * mm});
        }
    });
